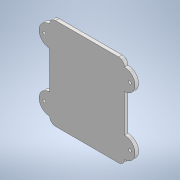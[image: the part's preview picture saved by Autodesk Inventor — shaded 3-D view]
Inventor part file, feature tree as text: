
AUTODESK INVENTOR PART (.ipt)
format: ipt  version: 2021 (Build 250183000, 183)  size: 147,968 bytes
history: native  units: mm
features: reference x11, other x3, extrude x2, sketch x2
ambient origin geometry x8: Origin, YZ Plane, XZ Plane, XY Plane, X Axis, Y Axis, Z Axis, Center Point
bodies: Body1 (feature_tree)
feature tree (18):
  extrude  "Extrusion3"  Depth=3.0mm
  extrude  "Extrusion4"  Depth=2.0mm TaperAngle=0.0deg
  sketch  "Sketch3"  dims[d6=3.0mm d7=0.0mm d8=0.2mm]
  reference  "Reference6"
  reference  "Reference7"
  reference  "Reference8"
  reference  "Reference9"
  sketch  "Sketch5"  dims[d9=1.0mm d10=2.0mm d11=0.0mm]
  reference  "Reference12"
  reference  "Reference13"
  reference  "Reference14"
  reference  "Reference15"
  reference  "Reference16"
  reference  "Reference17"
  reference  "Reference18"
  other  "<userpath>\Desktop\Motion_capture\MAIN\Models_3D\Arm_box\armbox_assembly.iam"
  other  "armbox_assembly.iam"
  other  "arm_box:1"
